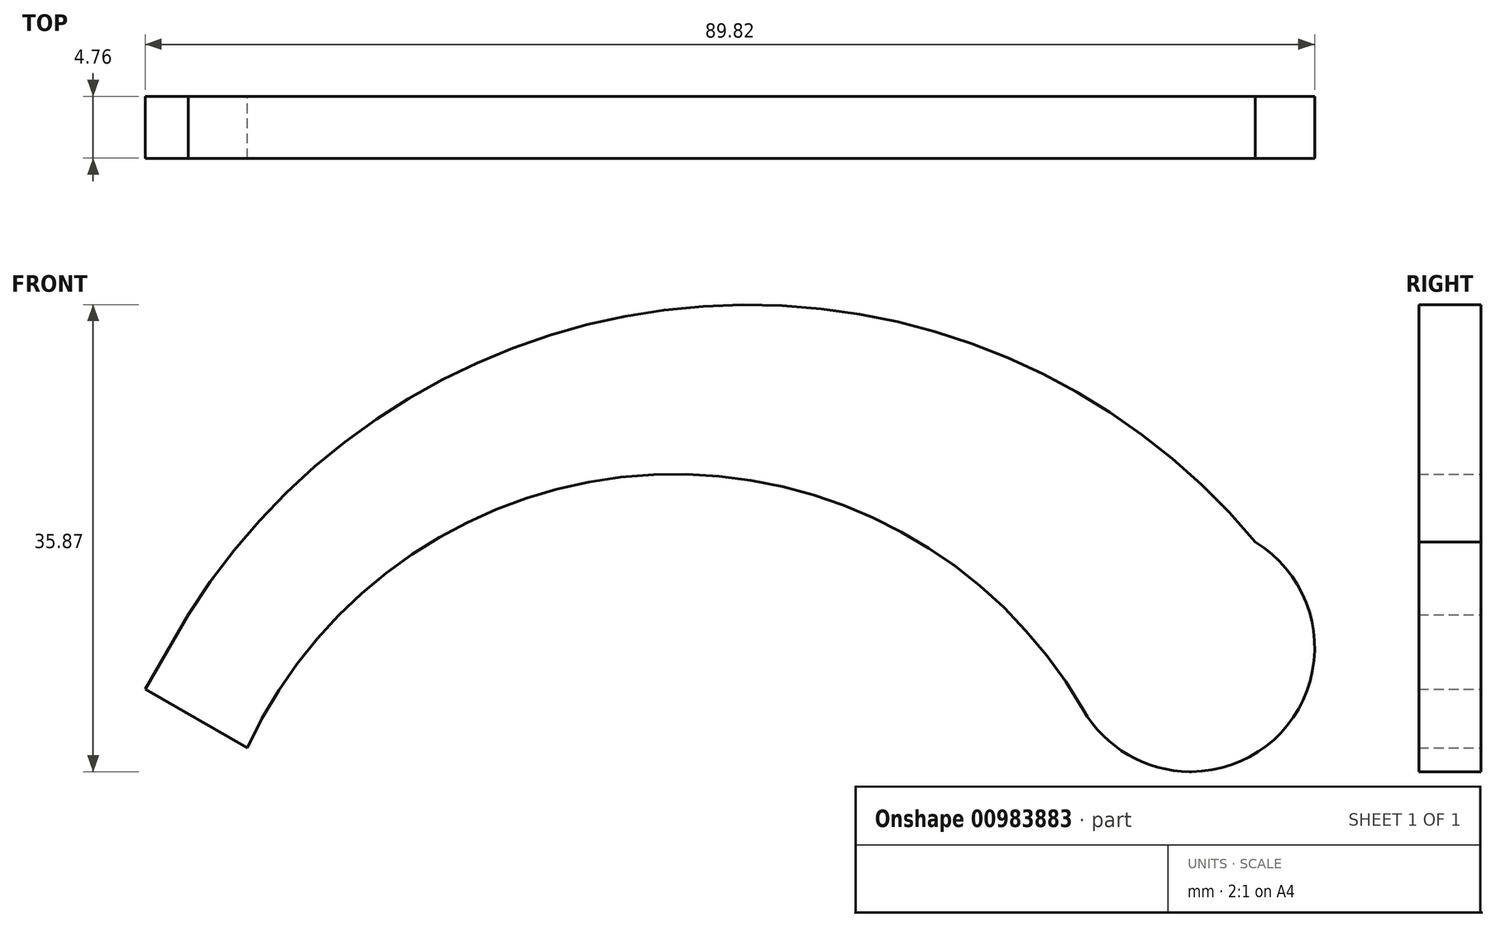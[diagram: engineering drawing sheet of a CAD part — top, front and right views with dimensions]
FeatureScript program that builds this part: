
annotation { "Feature Type Name" : "Feature", "Feature Type Description" : "" }
export const myFeature = defineFeature(function(context is Context, id is Id, definition is map)
    precondition{}
    {
        {
            var Q0;
            Q0=qCreatedBy(makeId("Front.planeOp"),FACE);
            var sketch = newSketch(context, id + "F0", { "sketchPlane" : qUnion([Q0])});
            skArc(sketch, "E0", {"start": v(31.35, 18.1) * mm, "mid": v(-1.65, 36.16) * mm, "end": v(-32.87, 15.16) * mm});
            skLineSegment(sketch, "E1", {"start": v(0, 0) * mm, "end": v(0, 36.2) * mm});
            skLineSegment(sketch, "E2", {"start": v(0, 0) * mm, "end": v(-31.35, 18.1) * mm});
            skLineSegment(sketch, "E3", {"start": v(0, 36.2) * mm, "end": v(0, 30.35) * mm});
            skLineSegment(sketch, "E4", {"start": v(-3.3, 30.35) * mm, "end": v(-3.3, 36.04) * mm});
            skLineSegment(sketch, "E5", {"start": v(3.3, 30.35) * mm, "end": v(3.3, 36.04) * mm});
            skLineSegment(sketch, "E6", {"start": v(-31.35, 18.1) * mm, "end": v(-26.29, 15.18) * mm});
            skLineSegment(sketch, "E7", {"start": v(-27.94, 12.32) * mm, "end": v(-32.87, 15.16) * mm});
            skLineSegment(sketch, "E8", {"start": v(-24.64, 18.04) * mm, "end": v(-29.56, 20.88) * mm});
            skLineSegment(sketch, "E9", {"start": v(0, 0) * mm, "end": v(31.35, 18.1) * mm});
            skLineSegment(sketch, "E10", {"start": v(-24.64, 18.04) * mm, "end": v(-37.4, 25.4) * mm});
            skLineSegment(sketch, "E11", {"start": v(0, 36.2) * mm, "end": v(0, 48.9) * mm});
            skLineSegment(sketch, "E12", {"start": v(-37.4, 25.4) * mm, "end": v(-32.87, 15.16) * mm});
            skLineSegment(sketch, "E13", {"start": v(3.3, 30.35) * mm, "end": v(-3.3, 30.35) * mm});
            skLineSegment(sketch, "E14", {"start": v(-24.64, 18.04) * mm, "end": v(-27.94, 12.32) * mm});
            skLineSegment(sketch, "E15", {"start": v(-32.87, 15.16) * mm, "end": v(-40.7, 19.68) * mm});
            skLineSegment(sketch, "E16", {"start": v(-37.4, 25.4) * mm, "end": v(-40.7, 19.68) * mm});
            skLineSegment(sketch, "E17", {"start": v(0, 0) * mm, "end": v(39.6, 22.86) * mm});
            skCircle(sketch, "E18", {"center": v(39.6, 22.86) * mm, "radius": 9.52 * mm});
            skArc(sketch, "E19", {"start": v(44.56, 30.99) * mm, "mid": v(2.16, 49.09) * mm, "end": v(-37.4, 25.4) * mm});
            skLineSegment(sketch, "E20", {"start": v(39.52, 13.34) * mm, "end": v(128.42, 13.34) * mm});
            skLineSegment(sketch, "E21", {"start": v(128.42, 13.34) * mm, "end": v(128.42, 32.39) * mm});
            skLineSegment(sketch, "E22", {"start": v(128.42, 32.39) * mm, "end": v(43.35, 32.39) * mm});
            skSolve(sketch);
        }
        {
            var Q0;
            {var subQ0=sQuery(id+"F0.wireOp",EDGE,"E20");Q0=makeQuery(id+"F0.imprint","IMPRINT",FACE,{"disambiguationData":[TD([[makeQuery(id+"F0.imprint","IMPRINT",EDGE,{"derivedFrom":subQ0}),1.0]])]});}
            var Q1;
            {var subQ0=sQuery(id+"F0.wireOp",EDGE,"E18");var subQ2=makeQuery(id+"F0.imprint","INTERSECT",VERTEX,{"derivedFrom":[subQ0,sQuery(id+"F0.wireOp",EDGE,"E19")]});Q1=makeQuery(id+"F0.imprint","IMPRINT",FACE,{"disambiguationData":[TD([[makeQuery(id+"F0.imprint","IMPRINT",EDGE,{"disambiguationData":[TD([[subQ2,1.0]])],"derivedFrom":subQ0}),1.0]])]});}
            var Q2;
            {var subQ5=sQuery(id+"F0.wireOp",EDGE,"E11");Q2=makeQuery(id+"F0.imprint","IMPRINT",FACE,{"disambiguationData":[TD([[makeQuery(id+"F0.imprint","IMPRINT",EDGE,{"derivedFrom":subQ5}),-1.0]])]});}
            var Q3;
            {var subQ0=sQuery(id+"F0.wireOp",EDGE,"E11");Q3=makeQuery(id+"F0.imprint","IMPRINT",FACE,{"disambiguationData":[TD([[makeQuery(id+"F0.imprint","IMPRINT",EDGE,{"derivedFrom":subQ0}),1.0]])]});}
            var Q4;
            Q4=makeQuery(id+"F0.imprint","IMPRINT",FACE,{"disambiguationData":[TD([[makeQuery(id+"F0.imprint","IMPRINT",EDGE,{"derivedFrom":sQuery(id+"F0.wireOp",EDGE,"E12")}),-1.0]])]});
            var Q5;
            {var subQ4=sQuery(id+"F0.wireOp",EDGE,"E12");Q5=makeQuery(id+"F0.imprint","IMPRINT",FACE,{"disambiguationData":[TD([[makeQuery(id+"F0.imprint","IMPRINT",EDGE,{"derivedFrom":subQ4}),1.0]])]});}
            var Q6;
            {var subQ0=sQuery(id+"F0.wireOp",EDGE,"E6");Q6=makeQuery(id+"F0.imprint","IMPRINT",FACE,{"disambiguationData":[TD([[makeQuery(id+"F0.imprint","IMPRINT",EDGE,{"derivedFrom":subQ0}),1.0]])]});}
            var Q7;
            {var subQ2=sQuery(id+"F0.wireOp",EDGE,"E6");Q7=makeQuery(id+"F0.imprint","IMPRINT",FACE,{"disambiguationData":[TD([[makeQuery(id+"F0.imprint","IMPRINT",EDGE,{"derivedFrom":subQ2}),-1.0]])]});}
            var Q8;
            {var subQ0=sQuery(id+"F0.wireOp",EDGE,"E3");Q8=makeQuery(id+"F0.imprint","IMPRINT",FACE,{"disambiguationData":[TD([[makeQuery(id+"F0.imprint","IMPRINT",EDGE,{"derivedFrom":subQ0}),-1.0]])]});}
            var Q9;
            {var subQ0=sQuery(id+"F0.wireOp",EDGE,"E3");Q9=makeQuery(id+"F0.imprint","IMPRINT",FACE,{"disambiguationData":[TD([[makeQuery(id+"F0.imprint","IMPRINT",EDGE,{"derivedFrom":subQ0}),1.0]])]});}
            extrude(context, id + "F1", {"entities" : qUnion([Q0, Q1, Q2, Q3, Q4, Q5, Q6, Q7, Q8, Q9]), "depth" : 4.76 * mm, "offsetDistance" : 25.4 * mm});
        }
    });
